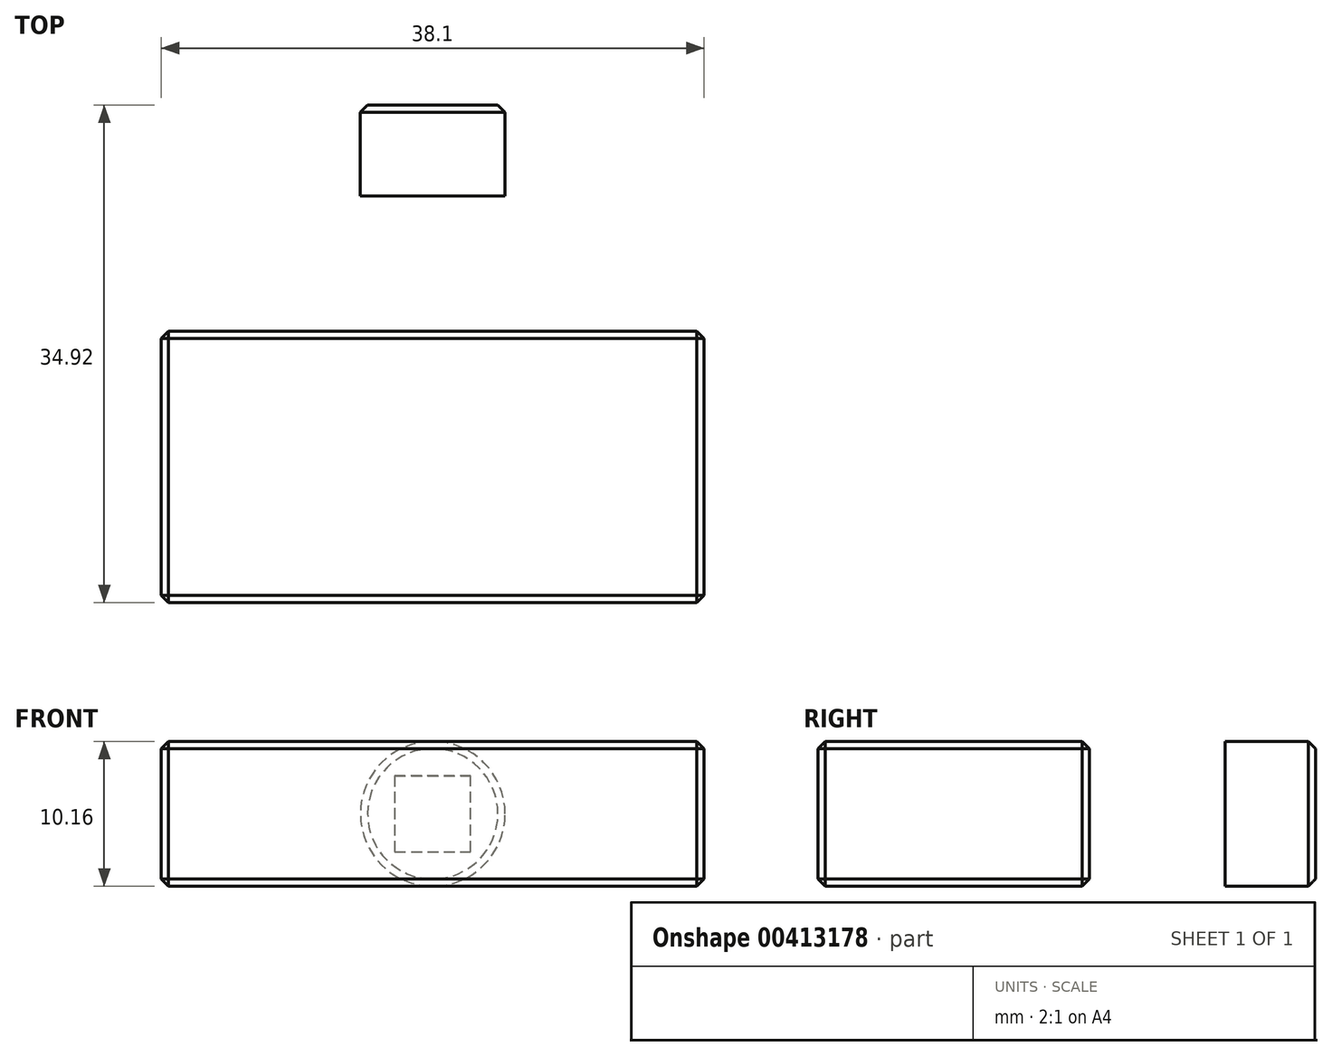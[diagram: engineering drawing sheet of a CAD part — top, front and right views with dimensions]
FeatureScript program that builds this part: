
annotation { "Feature Type Name" : "Feature", "Feature Type Description" : "" }
export const myFeature = defineFeature(function(context is Context, id is Id, definition is map)
    precondition{}
    {
        {
            var Q0;
            Q0=qCreatedBy(makeId("Front.planeOp"),FACE);
            var sketch = newSketch(context, id + "F0", { "sketchPlane" : qUnion([Q0])});
            skLineSegment(sketch, "E0.bottom", {"start": v(2.16, 2.16) * mm, "end": v(-2.16, 2.16) * mm});
            skLineSegment(sketch, "E0.top", {"start": v(2.16, -2.16) * mm, "end": v(-2.16, -2.16) * mm});
            skLineSegment(sketch, "E0.left", {"start": v(2.16, 2.16) * mm, "end": v(2.16, -2.16) * mm});
            skLineSegment(sketch, "E0.right", {"start": v(-2.16, 2.16) * mm, "end": v(-2.16, -2.16) * mm});
            skPoint(sketch, "E0.middle", {"position": v(0, 0) * mm});
            skCircle(sketch, "E1", {"center": v(0, 0) * mm, "radius": 5.08 * mm});
            skSolve(sketch);
        }
        {
            var Q0;
            Q0 = qSketchRegion(id + "F0", true);
            extrude(context, id + "F1", {"entities" : qUnion([Q0]), "depth" : 3 / 203.2 * mm});
        }
        {
            var Q0;
            Q0=makeQuery(id+"F1.opExtrude","CAP_FACE",FACE,{"disambiguationData":[OSD([sQuery(id+"F0.wireOp",EDGE,"E0.bottom"),sQuery(id+"F0.wireOp",EDGE,"E0.top"),sQuery(id+"F0.wireOp",EDGE,"E0.left"),sQuery(id+"F0.wireOp",EDGE,"E0.right"),sQuery(id+"F0.wireOp",EDGE,"E1")])],"isStart":false});
            var sketch = newSketch(context, id + "F2", { "sketchPlane" : qUnion([Q0])});
            skCircle(sketch, "E2", {"center": v(0, 0) * mm, "radius": 5.08 * mm});
            skSolve(sketch);
        }
        {
            var Q0;
            Q0 = qSketchRegion(id + "F2", true);
            extrude(context, id + "F3", {"entities" : qUnion([Q0]), "operationType" : NewBodyOperationType.ADD, "depth" : 6.35 * mm});
        }
        {
            var Q0;
            Q0=qCreatedBy(makeId("Top.planeOp"),FACE);
            var sketch = newSketch(context, id + "F4", { "sketchPlane" : qUnion([Q0])});
            skLineSegment(sketch, "E3.bottom", {"start": v(-19.05, -15.88) * mm, "end": v(19.05, -15.88) * mm});
            skLineSegment(sketch, "E3.top", {"start": v(-19.05, -34.93) * mm, "end": v(19.05, -34.93) * mm});
            skLineSegment(sketch, "E3.left", {"start": v(-19.05, -15.88) * mm, "end": v(-19.05, -34.93) * mm});
            skLineSegment(sketch, "E3.right", {"start": v(19.05, -15.88) * mm, "end": v(19.05, -34.93) * mm});
            skPoint(sketch, "E4", {"position": v(0, -15.88) * mm});
            skSolve(sketch);
        }
        {
            var Q0;
            Q0=makeQuery(id+"F4.imprint","IMPRINT",FACE,{"disambiguationData":[TD([[makeQuery(id+"F4.imprint","IMPRINT",EDGE,{"derivedFrom":sQuery(id+"F4.wireOp",EDGE,"E3.bottom")}),-1.0]])]});
            extrude(context, id + "F5", {"entities" : qUnion([Q0]), "operationType" : NewBodyOperationType.ADD, "endBound" : BoundingType.SYMMETRIC, "depth" : 10.16 * mm});
        }
        {
            var Q0;
            Q0=makeQuery(id+"F5.opExtrude","SWEPT_FACE",FACE,{"disambiguationData":[OSD([sQuery(id+"F4.wireOp",EDGE,"E3.top")])]});
            var Q1;
            Q1=makeQuery(id+"F5.opExtrude","CAP_EDGE",EDGE,{"disambiguationData":[OSD([sQuery(id+"F4.wireOp",EDGE,"E3.right")])],"isStart":false});
            var Q2;
            Q2=makeQuery(id+"F5.opExtrude","CAP_EDGE",EDGE,{"disambiguationData":[OSD([sQuery(id+"F4.wireOp",EDGE,"E3.right")])],"isStart":true});
            var Q3;
            Q3=makeQuery(id+"F5.opExtrude","CAP_EDGE",EDGE,{"disambiguationData":[OSD([sQuery(id+"F4.wireOp",EDGE,"E3.left")])],"isStart":false});
            var Q4;
            Q4=makeQuery(id+"F5.opExtrude","CAP_EDGE",EDGE,{"disambiguationData":[OSD([sQuery(id+"F4.wireOp",EDGE,"E3.left")])],"isStart":true});
            var Q5;
            Q5=makeQuery(id+"F1.opExtrude","CAP_FACE",FACE,{"disambiguationData":[OSD([sQuery(id+"F0.wireOp",EDGE,"E0.bottom"),sQuery(id+"F0.wireOp",EDGE,"E0.top"),sQuery(id+"F0.wireOp",EDGE,"E0.left"),sQuery(id+"F0.wireOp",EDGE,"E0.right"),sQuery(id+"F0.wireOp",EDGE,"E1")])],"isStart":true});
            var Q6;
            Q6=makeQuery(id+"F5.opExtrude","SWEPT_EDGE",EDGE,{"disambiguationData":[OSD([sQuery(id+"F4.wireOp",EDGE,"E3.bottom"),sQuery(id+"F4.wireOp",EDGE,"E3.right")])]});
            var Q7;
            {var subQ0=sQuery(id+"F4.wireOp",EDGE,"E3.right");var subQ1=sQuery(id+"F4.wireOp",EDGE,"E3.bottom");Q7=makeQuery(id+"F5.boolean.opBoolean","SPLIT",EDGE,{"disambiguationData":[TD([makeQuery(id+"F5.opExtrude","SWEPT_FACE",FACE,{"disambiguationData":[OSD([subQ0])]})])],"derivedFrom":makeQuery(id+"F5.opExtrude","CAP_EDGE",EDGE,{"disambiguationData":[OSD([subQ1])],"isStart":false})});}
            var Q8;
            {var subQ0=sQuery(id+"F4.wireOp",EDGE,"E3.bottom");var subQ1=sQuery(id+"F4.wireOp",EDGE,"E3.right");Q8=makeQuery(id+"F5.boolean.opBoolean","SPLIT",EDGE,{"disambiguationData":[TD([makeQuery(id+"F5.opExtrude","SWEPT_FACE",FACE,{"disambiguationData":[OSD([subQ1])]})])],"derivedFrom":makeQuery(id+"F5.opExtrude","CAP_EDGE",EDGE,{"disambiguationData":[OSD([subQ0])],"isStart":true})});}
            var Q9;
            Q9=makeQuery(id+"F5.opExtrude","SWEPT_EDGE",EDGE,{"disambiguationData":[OSD([sQuery(id+"F4.wireOp",EDGE,"E3.bottom"),sQuery(id+"F4.wireOp",EDGE,"E3.left")])]});
            chamfer(context, id + "F6", {"entities" : qUnion([Q0, Q1, Q2, Q3, Q4, Q5, Q6, Q7, Q8, Q9]), "width" : 0.5 * mm, "tangentPropagation" : true});
        }
    });
